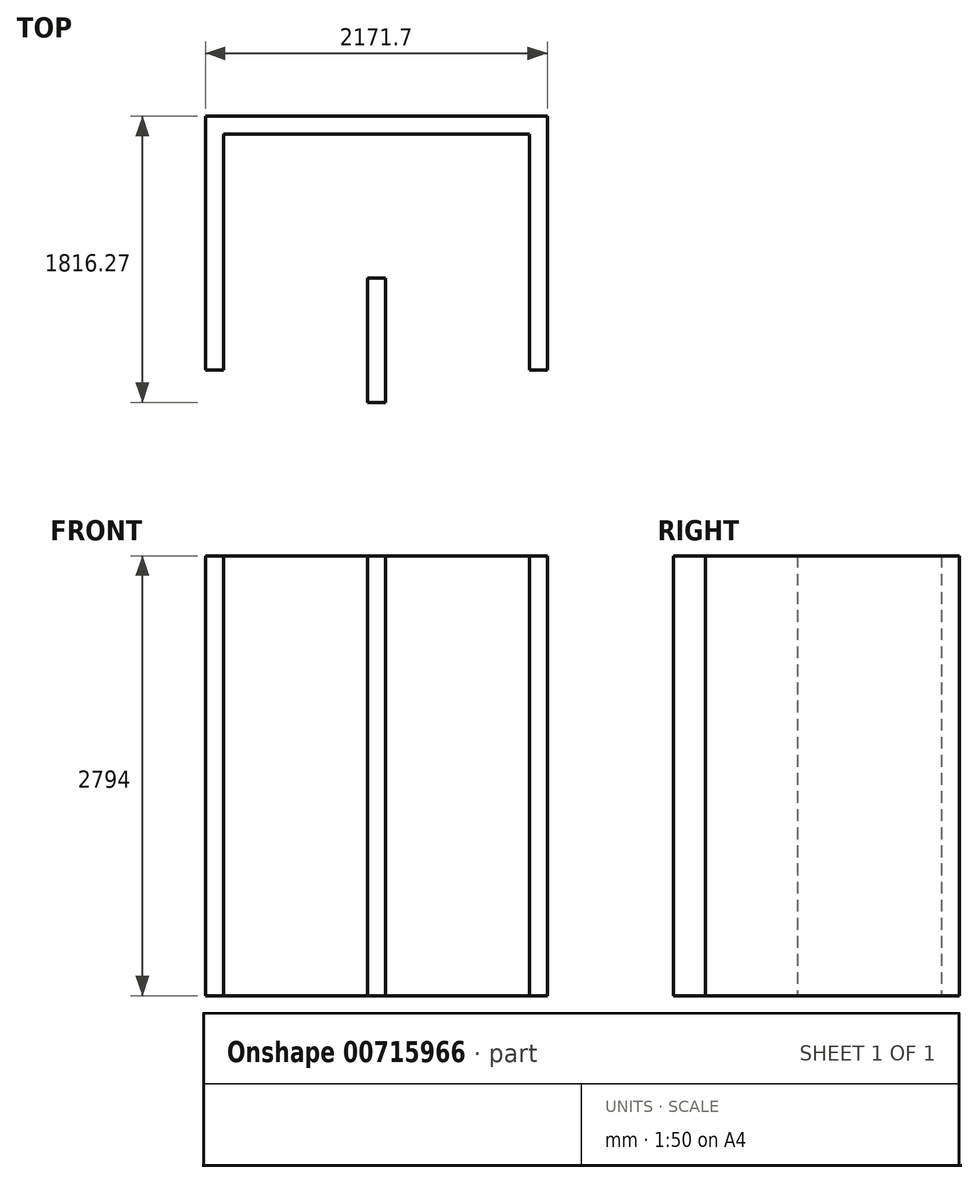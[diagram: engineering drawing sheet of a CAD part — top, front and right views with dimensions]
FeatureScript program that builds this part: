
annotation { "Feature Type Name" : "Feature", "Feature Type Description" : "" }
export const myFeature = defineFeature(function(context is Context, id is Id, definition is map)
    precondition{}
    {
        {
            var Q0;
            Q0=qCreatedBy(makeId("Top.planeOp"),FACE);
            var sketch = newSketch(context, id + "F0", { "sketchPlane" : qUnion([Q0])});
            skLineSegment(sketch, "E0", {"start": v(-648.55, 520.62) * mm, "end": v(1294.55, 520.62) * mm});
            skLineSegment(sketch, "E1", {"start": v(1294.55, 520.62) * mm, "end": v(1294.55, -977.98) * mm});
            skLineSegment(sketch, "E2", {"start": v(-648.55, 520.62) * mm, "end": v(-648.55, -977.98) * mm});
            skLineSegment(sketch, "E3", {"start": v(-648.55, -977.98) * mm, "end": v(-762.85, -977.98) * mm});
            skLineSegment(sketch, "E4", {"start": v(-762.85, -977.98) * mm, "end": v(-762.85, 634.92) * mm});
            skLineSegment(sketch, "E5", {"start": v(-762.85, 634.92) * mm, "end": v(1408.85, 634.92) * mm});
            skLineSegment(sketch, "E6", {"start": v(1408.85, 634.92) * mm, "end": v(1408.85, -977.98) * mm});
            skLineSegment(sketch, "E7", {"start": v(1408.85, -977.98) * mm, "end": v(1294.55, -977.98) * mm});
            skLineSegment(sketch, "E8.bottom", {"start": v(265.85, -393.78) * mm, "end": v(380.15, -393.78) * mm});
            skLineSegment(sketch, "E8.top", {"start": v(265.85, -1181.35) * mm, "end": v(380.15, -1181.35) * mm});
            skLineSegment(sketch, "E8.left", {"start": v(265.85, -393.78) * mm, "end": v(265.85, -1181.35) * mm});
            skLineSegment(sketch, "E8.right", {"start": v(380.15, -393.78) * mm, "end": v(380.15, -1181.35) * mm});
            skLineSegment(sketch, "E9", {"start": v(323, 520.62) * mm, "end": v(323, -393.78) * mm});
            skPoint(sketch, "E9.endSnap0", {"position": v(323, 634.92) * mm});
            skLineSegment(sketch, "E10", {"start": v(323, -393.78) * mm, "end": v(323, -670.53) * mm});
            skPoint(sketch, "E10.endSnap0", {"position": v(323, -393.78) * mm});
            skSolve(sketch);
        }
        {
            var Q0;
            Q0=makeQuery(id+"F0.imprint","IMPRINT",FACE,{"disambiguationData":[TD([[makeQuery(id+"F0.imprint","IMPRINT",EDGE,{"derivedFrom":sQuery(id+"F0.wireOp",EDGE,"E0")}),1.0]])]});
            var Q1;
            Q1=makeQuery(id+"F0.imprint","IMPRINT",FACE,{"disambiguationData":[TD([[makeQuery(id+"F0.imprint","IMPRINT",EDGE,{"derivedFrom":sQuery(id+"F0.wireOp",EDGE,"E8.top")}),1.0]])]});
            var Q2;
            Q2=sQuery(id+"F0.wireOp",EDGE,"E6");
            var Q3;
            Q3=sQuery(id+"F0.wireOp",EDGE,"E1");
            var Q4;
            Q4=sQuery(id+"F0.wireOp",EDGE,"E0");
            var Q5;
            Q5=sQuery(id+"F0.wireOp",EDGE,"E5");
            var Q6;
            Q6=sQuery(id+"F0.wireOp",EDGE,"E2");
            var Q7;
            Q7=sQuery(id+"F0.wireOp",EDGE,"E4");
            var Q8;
            Q8=sQuery(id+"F0.wireOp",EDGE,"E3");
            var Q9;
            Q9=sQuery(id+"F0.wireOp",EDGE,"E7");
            extrude(context, id + "F1", {"entities" : qUnion([Q0, Q1]), "surfaceEntities" : qUnion([Q2, Q3, Q4, Q5, Q6, Q7, Q8, Q9]), "depth" : 2794 * mm, "offsetDistance" : 25.4 * mm});
        }
    });
